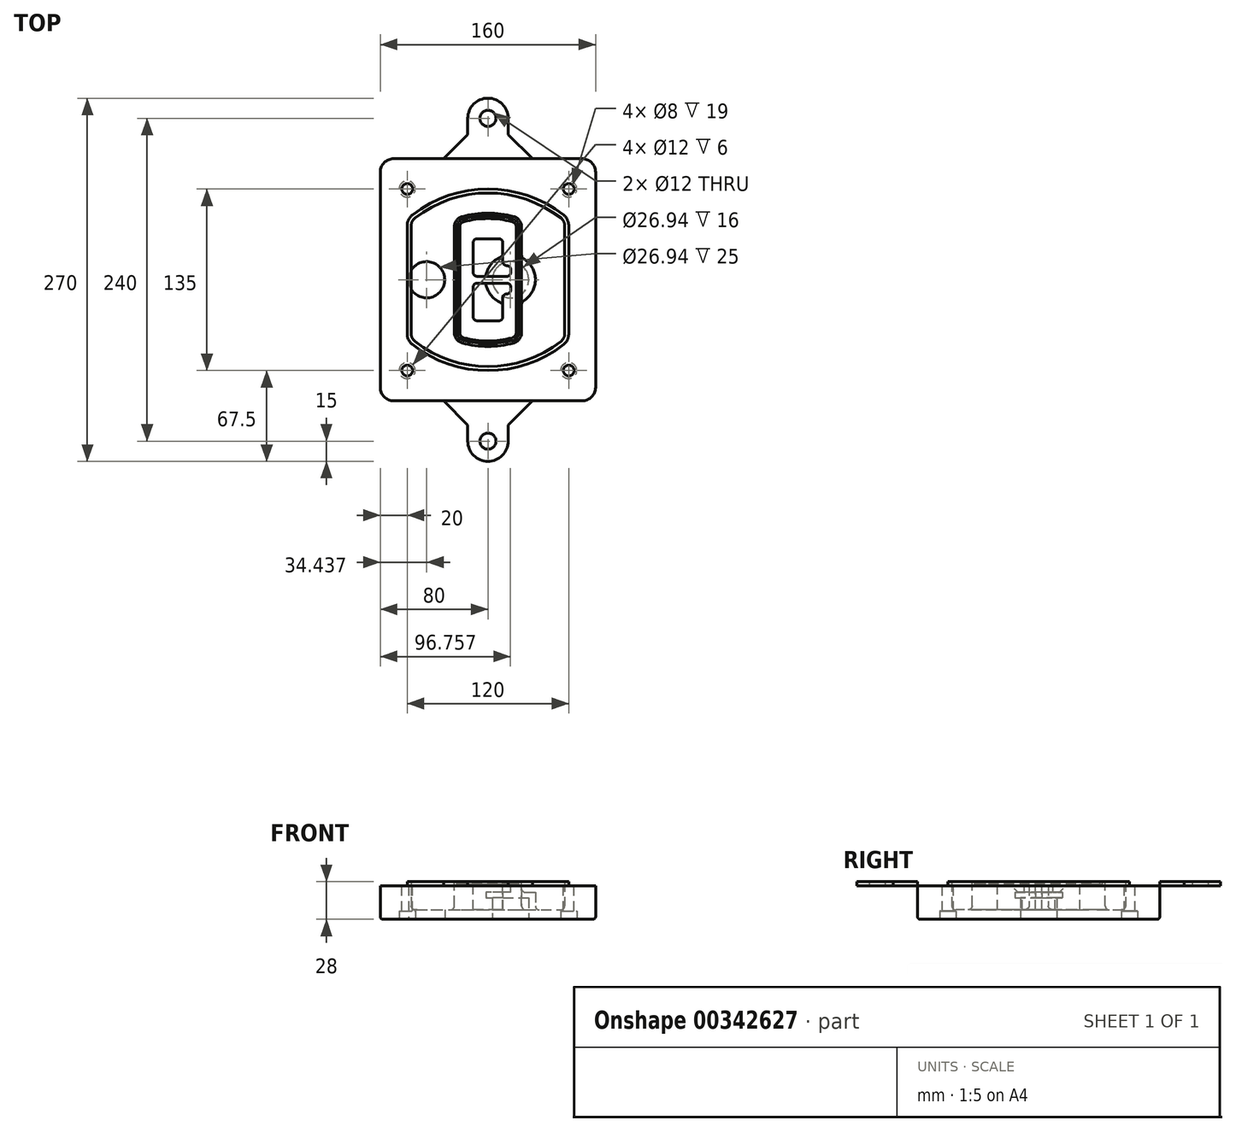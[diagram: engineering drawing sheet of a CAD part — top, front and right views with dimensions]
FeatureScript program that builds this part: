
annotation { "Feature Type Name" : "Feature", "Feature Type Description" : "" }
export const myFeature = defineFeature(function(context is Context, id is Id, definition is map)
    precondition{}
    {
        {
            var Q0;
            Q0=qCreatedBy(makeId("Top.planeOp"),FACE);
            var sketch = newSketch(context, id + "F0", { "sketchPlane" : qUnion([Q0])});
            skPoint(sketch, "E0.rect.middle", {"position": v(0, 0) * mm});
            skLineSegment(sketch, "E1.bottom", {"start": v(-70, -90) * mm, "end": v(70, -90) * mm});
            skLineSegment(sketch, "E1.top", {"start": v(-70, 90) * mm, "end": v(70, 90) * mm});
            skLineSegment(sketch, "E1.left", {"start": v(-80, -80) * mm, "end": v(-80, 80) * mm});
            skLineSegment(sketch, "E1.right", {"start": v(80, -80) * mm, "end": v(80, 80) * mm});
            skLineSegment(sketch, "E2", {"start": v(-80, 90) * mm, "end": v(80, -90) * mm, "construction": true});
            skLineSegment(sketch, "E3", {"start": v(80, 90) * mm, "end": v(-80, -90) * mm, "construction": true});
            skCircle(sketch, "E4", {"center": v(-60, 67.5) * mm, "radius": 4 * mm});
            skCircle(sketch, "E5", {"center": v(60, 67.5) * mm, "radius": 4 * mm});
            skCircle(sketch, "E6", {"center": v(60, -67.5) * mm, "radius": 4 * mm});
            skCircle(sketch, "E7", {"center": v(-60, -67.5) * mm, "radius": 4 * mm});
            skLineSegment(sketch, "E8", {"start": v(-60, 67.5) * mm, "end": v(60, 67.5) * mm, "construction": true});
            skLineSegment(sketch, "E9", {"start": v(60, 67.5) * mm, "end": v(60, -67.5) * mm, "construction": true});
            skLineSegment(sketch, "E10", {"start": v(60, -67.5) * mm, "end": v(-60, -67.5) * mm, "construction": true});
            skLineSegment(sketch, "E11", {"start": v(-60, -67.5) * mm, "end": v(-60, 67.5) * mm, "construction": true});
            skLineSegment(sketch, "E12", {"start": v(-60, 40.3) * mm, "end": v(-60, -40.3) * mm});
            skLineSegment(sketch, "E13", {"start": v(60, 40.3) * mm, "end": v(60, -40.3) * mm});
            skArc(sketch, "E14", {"start": v(56.15, 48.18) * mm, "mid": v(0, 67.5) * mm, "end": v(-56.15, 48.18) * mm});
            skArc(sketch, "E15", {"start": v(-56.15, -48.18) * mm, "mid": v(0, -67.5) * mm, "end": v(56.15, -48.18) * mm});
            skLineSegment(sketch, "E16", {"start": v(-60, 0) * mm, "end": v(60, 0) * mm, "construction": true});
            skPoint(sketch, "E17.visualSharp", {"position": v(-60, -45) * mm});
            skArc(sketch, "E17.filletArc", {"start": v(-60, -40.3) * mm, "mid": v(-58.99, -44.68) * mm, "end": v(-56.15, -48.18) * mm});
            skPoint(sketch, "E18.visualSharp", {"position": v(-60, 45) * mm});
            skArc(sketch, "E18.filletArc", {"start": v(-56.15, 48.18) * mm, "mid": v(-58.99, 44.68) * mm, "end": v(-60, 40.3) * mm});
            skPoint(sketch, "E19.visualSharp", {"position": v(60, 45) * mm});
            skArc(sketch, "E19.filletArc", {"start": v(60, 40.3) * mm, "mid": v(58.99, 44.68) * mm, "end": v(56.15, 48.18) * mm});
            skPoint(sketch, "E20.visualSharp", {"position": v(60, -45) * mm});
            skArc(sketch, "E20.filletArc", {"start": v(56.15, -48.18) * mm, "mid": v(58.99, -44.68) * mm, "end": v(60, -40.3) * mm});
            skPoint(sketch, "E21.visualSharp", {"position": v(-80, 90) * mm});
            skArc(sketch, "E21.filletArc", {"start": v(-70, 90) * mm, "mid": v(-77.07, 87.07) * mm, "end": v(-80, 80) * mm});
            skPoint(sketch, "E22.visualSharp", {"position": v(80, 90) * mm});
            skArc(sketch, "E22.filletArc", {"start": v(80, 80) * mm, "mid": v(77.07, 87.07) * mm, "end": v(70, 90) * mm});
            skPoint(sketch, "E23.visualSharp", {"position": v(80, -90) * mm});
            skArc(sketch, "E23.filletArc", {"start": v(70, -90) * mm, "mid": v(77.07, -87.07) * mm, "end": v(80, -80) * mm});
            skPoint(sketch, "E24.visualSharp", {"position": v(-80, -90) * mm});
            skArc(sketch, "E24.filletArc", {"start": v(-80, -80) * mm, "mid": v(-77.07, -87.07) * mm, "end": v(-70, -90) * mm});
            skArc(sketch, "E25.0", {"start": v(57, 40.3) * mm, "mid": v(56.3, 43.36) * mm, "end": v(54.3, 45.81) * mm});
            skLineSegment(sketch, "E25.1", {"start": v(57, 40.3) * mm, "end": v(57, -40.3) * mm});
            skArc(sketch, "E25.2", {"start": v(54.3, -45.81) * mm, "mid": v(56.3, -43.36) * mm, "end": v(57, -40.3) * mm});
            skArc(sketch, "E25.3", {"start": v(-54.3, -45.81) * mm, "mid": v(0, -64.5) * mm, "end": v(54.3, -45.81) * mm});
            skArc(sketch, "E25.4", {"start": v(-57, -40.3) * mm, "mid": v(-56.3, -43.36) * mm, "end": v(-54.3, -45.81) * mm});
            skArc(sketch, "E25.5", {"start": v(54.3, 45.81) * mm, "mid": v(0, 64.5) * mm, "end": v(-54.3, 45.81) * mm});
            skLineSegment(sketch, "E25.6", {"start": v(-57, 40.3) * mm, "end": v(-57, -40.3) * mm});
            skArc(sketch, "E25.7", {"start": v(-54.3, 45.81) * mm, "mid": v(-56.3, 43.36) * mm, "end": v(-57, 40.3) * mm});
            skArc(sketch, "E26.0", {"start": v(-58.62, 51.33) * mm, "mid": v(-62.58, 46.43) * mm, "end": v(-64, 40.3) * mm});
            skArc(sketch, "E26.1", {"start": v(58.62, 51.33) * mm, "mid": v(0, 71.5) * mm, "end": v(-58.62, 51.33) * mm});
            skArc(sketch, "E26.2", {"start": v(64, 40.3) * mm, "mid": v(62.58, 46.43) * mm, "end": v(58.62, 51.33) * mm});
            skLineSegment(sketch, "E26.3", {"start": v(64, 40.3) * mm, "end": v(64, -40.3) * mm});
            skArc(sketch, "E26.4", {"start": v(58.62, -51.33) * mm, "mid": v(62.58, -46.43) * mm, "end": v(64, -40.3) * mm});
            skLineSegment(sketch, "E26.5", {"start": v(-64, 40.3) * mm, "end": v(-64, -40.3) * mm});
            skArc(sketch, "E26.6", {"start": v(-58.62, -51.33) * mm, "mid": v(0, -71.5) * mm, "end": v(58.62, -51.33) * mm});
            skArc(sketch, "E26.7", {"start": v(-64, -40.3) * mm, "mid": v(-62.58, -46.43) * mm, "end": v(-58.62, -51.33) * mm});
            skSolve(sketch);
        }
        {
            var Q0;
            Q0=makeQuery(id+"F0.imprint","IMPRINT",FACE,{"disambiguationData":[TD([[makeQuery(id+"F0.imprint","IMPRINT",EDGE,{"derivedFrom":sQuery(id+"F0.wireOp",EDGE,"E1.bottom")}),1.0]])]});
            var Q1;
            Q1=makeQuery(id+"F0.imprint","IMPRINT",FACE,{"disambiguationData":[TD([[makeQuery(id+"F0.imprint","IMPRINT",EDGE,{"derivedFrom":sQuery(id+"F0.wireOp",EDGE,"E12")}),1.0]])]});
            var Q2;
            Q2=makeQuery(id+"F0.imprint","IMPRINT",FACE,{"disambiguationData":[TD([[makeQuery(id+"F0.imprint","IMPRINT",EDGE,{"derivedFrom":sQuery(id+"F0.wireOp",EDGE,"E25.0")}),1.0]])]});
            var Q3;
            Q3=makeQuery(id+"F0.imprint","IMPRINT",FACE,{"disambiguationData":[TD([[makeQuery(id+"F0.imprint","IMPRINT",EDGE,{"derivedFrom":sQuery(id+"F0.wireOp",EDGE,"E12")}),-1.0]])]});
            extrude(context, id + "F1", {"entities" : qUnion([Q0, Q1, Q2, Q3]), "oppositeDirection" : true, "depth" : 25 * mm});
        }
        {
            var Q0;
            Q0=makeQuery(id+"F0.imprint","IMPRINT",FACE,{"disambiguationData":[TD([[makeQuery(id+"F0.imprint","IMPRINT",EDGE,{"derivedFrom":sQuery(id+"F0.wireOp",EDGE,"E12")}),1.0]])]});
            extrude(context, id + "F2", {"entities" : qUnion([Q0]), "operationType" : NewBodyOperationType.ADD, "depth" : 3 * mm});
        }
        {
            var Q0;
            Q0=makeQuery(id+"F0.imprint","IMPRINT",FACE,{"disambiguationData":[TD([[makeQuery(id+"F0.imprint","IMPRINT",EDGE,{"derivedFrom":sQuery(id+"F0.wireOp",EDGE,"E25.0")}),1.0]])]});
            extrude(context, id + "F3", {"entities" : qUnion([Q0]), "operationType" : NewBodyOperationType.REMOVE, "oppositeDirection" : true, "depth" : 18 * mm});
        }
        {
            var Q0;
            Q0=makeQuery(id+"F2.opExtrude","CAP_FACE",FACE,{"disambiguationData":[OSD([sQuery(id+"F0.wireOp",EDGE,"E12"),sQuery(id+"F0.wireOp",EDGE,"E13"),sQuery(id+"F0.wireOp",EDGE,"E14"),sQuery(id+"F0.wireOp",EDGE,"E15"),sQuery(id+"F0.wireOp",EDGE,"E17.filletArc"),sQuery(id+"F0.wireOp",EDGE,"E18.filletArc"),sQuery(id+"F0.wireOp",EDGE,"E19.filletArc"),sQuery(id+"F0.wireOp",EDGE,"E20.filletArc"),sQuery(id+"F0.wireOp",EDGE,"E25.0"),sQuery(id+"F0.wireOp",EDGE,"E25.1"),sQuery(id+"F0.wireOp",EDGE,"E25.2"),sQuery(id+"F0.wireOp",EDGE,"E25.3"),sQuery(id+"F0.wireOp",EDGE,"E25.4"),sQuery(id+"F0.wireOp",EDGE,"E25.5"),sQuery(id+"F0.wireOp",EDGE,"E25.6"),sQuery(id+"F0.wireOp",EDGE,"E25.7")])],"isStart":false});
            var sketch = newSketch(context, id + "F4", { "sketchPlane" : qUnion([Q0])});
            skArc(sketch, "E27.0", {"start": v(-19.08, -46.97) * mm, "mid": v(0, -49.5) * mm, "end": v(19.08, -46.97) * mm});
            skArc(sketch, "E28.0", {"start": v(19.08, 46.97) * mm, "mid": v(0, 49.5) * mm, "end": v(-19.08, 46.97) * mm});
            skLineSegment(sketch, "E29", {"start": v(-25, 39.25) * mm, "end": v(-25, -39.25) * mm});
            skLineSegment(sketch, "E30", {"start": v(25, 39.25) * mm, "end": v(25, -39.25) * mm});
            skLineSegment(sketch, "E31", {"start": v(-25, 45.1) * mm, "end": v(25, 45.1) * mm, "construction": true});
            skLineSegment(sketch, "E32", {"start": v(-25, -45.1) * mm, "end": v(25, -45.1) * mm, "construction": true});
            skPoint(sketch, "E33.visualSharp", {"position": v(-25, 45.1) * mm});
            skArc(sketch, "E33.filletArc", {"start": v(-19.08, 46.97) * mm, "mid": v(-23.35, 44.11) * mm, "end": v(-25, 39.25) * mm});
            skPoint(sketch, "E34.visualSharp", {"position": v(25, 45.1) * mm});
            skArc(sketch, "E34.filletArc", {"start": v(25, 39.25) * mm, "mid": v(23.35, 44.11) * mm, "end": v(19.08, 46.97) * mm});
            skPoint(sketch, "E35.visualSharp", {"position": v(25, -45.1) * mm});
            skArc(sketch, "E35.filletArc", {"start": v(19.08, -46.97) * mm, "mid": v(23.35, -44.11) * mm, "end": v(25, -39.25) * mm});
            skPoint(sketch, "E36.visualSharp", {"position": v(-25, -45.1) * mm});
            skArc(sketch, "E36.filletArc", {"start": v(-25, -39.25) * mm, "mid": v(-23.35, -44.11) * mm, "end": v(-19.08, -46.97) * mm});
            skArc(sketch, "E37.0", {"start": v(54.3, 45.81) * mm, "mid": v(0, 64.5) * mm, "end": v(-54.3, 45.81) * mm});
            skArc(sketch, "E37.1", {"start": v(-54.3, 45.81) * mm, "mid": v(-56.3, 43.36) * mm, "end": v(-57, 40.3) * mm});
            skLineSegment(sketch, "E37.2", {"start": v(-57, 40.3) * mm, "end": v(-57, -40.3) * mm});
            skArc(sketch, "E37.3", {"start": v(-57, -40.3) * mm, "mid": v(-56.3, -43.36) * mm, "end": v(-54.3, -45.81) * mm});
            skArc(sketch, "E37.4", {"start": v(-54.3, -45.81) * mm, "mid": v(0, -64.5) * mm, "end": v(54.3, -45.81) * mm});
            skArc(sketch, "E37.5", {"start": v(54.3, -45.81) * mm, "mid": v(56.3, -43.36) * mm, "end": v(57, -40.3) * mm});
            skLineSegment(sketch, "E37.6", {"start": v(57, 40.3) * mm, "end": v(57, -40.3) * mm});
            skArc(sketch, "E37.7", {"start": v(57, 40.3) * mm, "mid": v(56.3, 43.36) * mm, "end": v(54.3, 45.81) * mm});
            skLineSegment(sketch, "E38.0", {"start": v(23, 39.25) * mm, "end": v(23, -39.25) * mm});
            skArc(sketch, "E38.1", {"start": v(18.56, -45.04) * mm, "mid": v(21.76, -42.9) * mm, "end": v(23, -39.25) * mm});
            skArc(sketch, "E38.2", {"start": v(-18.56, -45.04) * mm, "mid": v(0, -47.5) * mm, "end": v(18.56, -45.04) * mm});
            skArc(sketch, "E38.3", {"start": v(-23, -39.25) * mm, "mid": v(-21.76, -42.9) * mm, "end": v(-18.56, -45.04) * mm});
            skLineSegment(sketch, "E38.4", {"start": v(-23, 39.25) * mm, "end": v(-23, -39.25) * mm});
            skArc(sketch, "E38.5", {"start": v(23, 39.25) * mm, "mid": v(21.76, 42.9) * mm, "end": v(18.56, 45.04) * mm});
            skArc(sketch, "E38.6", {"start": v(-18.56, 45.04) * mm, "mid": v(-21.76, 42.9) * mm, "end": v(-23, 39.25) * mm});
            skArc(sketch, "E38.7", {"start": v(18.56, 45.04) * mm, "mid": v(0, 47.5) * mm, "end": v(-18.56, 45.04) * mm});
            skArc(sketch, "E39.0", {"start": v(21, 39.25) * mm, "mid": v(20.18, 41.68) * mm, "end": v(18.04, 43.1) * mm});
            skLineSegment(sketch, "E39.1", {"start": v(21, 39.25) * mm, "end": v(21, -39.25) * mm});
            skArc(sketch, "E39.2", {"start": v(18.04, -43.1) * mm, "mid": v(20.18, -41.68) * mm, "end": v(21, -39.25) * mm});
            skArc(sketch, "E39.3", {"start": v(-18.04, -43.1) * mm, "mid": v(0, -45.5) * mm, "end": v(18.04, -43.1) * mm});
            skArc(sketch, "E39.4", {"start": v(-21, -39.25) * mm, "mid": v(-20.18, -41.68) * mm, "end": v(-18.04, -43.1) * mm});
            skArc(sketch, "E39.5", {"start": v(18.04, 43.1) * mm, "mid": v(0, 45.5) * mm, "end": v(-18.04, 43.1) * mm});
            skLineSegment(sketch, "E39.6", {"start": v(-21, 39.25) * mm, "end": v(-21, -39.25) * mm});
            skArc(sketch, "E39.7", {"start": v(-18.04, 43.1) * mm, "mid": v(-20.18, 41.68) * mm, "end": v(-21, 39.25) * mm});
            skLineSegment(sketch, "E40", {"start": v(-25, 0) * mm, "end": v(25, 0) * mm, "construction": true});
            skLineSegment(sketch, "E41", {"start": v(-11, 5.5) * mm, "end": v(-11, 27.5) * mm});
            skLineSegment(sketch, "E42", {"start": v(-8, 30.5) * mm, "end": v(8, 30.5) * mm});
            skLineSegment(sketch, "E43", {"start": v(11, 27.5) * mm, "end": v(11, 13.5) * mm});
            skLineSegment(sketch, "E44", {"start": v(14, 10.5) * mm, "end": v(14, 10.5) * mm});
            skLineSegment(sketch, "E45", {"start": v(17, 7.5) * mm, "end": v(17, 5.5) * mm});
            skLineSegment(sketch, "E46", {"start": v(14, 2.5) * mm, "end": v(-8, 2.5) * mm});
            skPoint(sketch, "E47.visualSharp", {"position": v(-11, 30.5) * mm});
            skArc(sketch, "E47.filletArc", {"start": v(-8, 30.5) * mm, "mid": v(-10.12, 29.62) * mm, "end": v(-11, 27.5) * mm});
            skPoint(sketch, "E48.visualSharp", {"position": v(11, 30.5) * mm});
            skArc(sketch, "E48.filletArc", {"start": v(11, 27.5) * mm, "mid": v(10.12, 29.62) * mm, "end": v(8, 30.5) * mm});
            skPoint(sketch, "E49.visualSharp", {"position": v(11, 10.5) * mm});
            skArc(sketch, "E49.filletArc", {"start": v(11, 13.5) * mm, "mid": v(11.88, 11.38) * mm, "end": v(14, 10.5) * mm});
            skPoint(sketch, "E50.visualSharp", {"position": v(17, 10.5) * mm});
            skArc(sketch, "E50.filletArc", {"start": v(17, 7.5) * mm, "mid": v(16.12, 9.62) * mm, "end": v(14, 10.5) * mm});
            skPoint(sketch, "E51.visualSharp", {"position": v(17, 2.5) * mm});
            skArc(sketch, "E51.filletArc", {"start": v(14, 2.5) * mm, "mid": v(16.12, 3.38) * mm, "end": v(17, 5.5) * mm});
            skPoint(sketch, "E52.visualSharp", {"position": v(-11, 2.5) * mm});
            skArc(sketch, "E52.filletArc", {"start": v(-11, 5.5) * mm, "mid": v(-10.12, 3.38) * mm, "end": v(-8, 2.5) * mm});
            skLineSegment(sketch, "E53.0.MirrorCS", {"start": v(14, -2.5) * mm, "end": v(-8, -2.5) * mm});
            skArc(sketch, "E54.0.MirrorCS", {"start": v(-11, -5.5) * mm, "mid": v(-10.12, -3.38) * mm, "end": v(-8, -2.5) * mm});
            skLineSegment(sketch, "E55.0.MirrorCS", {"start": v(-11, -5.5) * mm, "end": v(-11, -27.5) * mm});
            skArc(sketch, "E56.0.MirrorCS", {"start": v(-8, -30.5) * mm, "mid": v(-10.12, -29.62) * mm, "end": v(-11, -27.5) * mm});
            skLineSegment(sketch, "E57.0.MirrorCS", {"start": v(-8, -30.5) * mm, "end": v(8, -30.5) * mm});
            skArc(sketch, "E58.0.MirrorCS", {"start": v(11, -27.5) * mm, "mid": v(10.12, -29.62) * mm, "end": v(8, -30.5) * mm});
            skLineSegment(sketch, "E59.0.MirrorCS", {"start": v(11, -27.5) * mm, "end": v(11, -13.5) * mm});
            skArc(sketch, "E60.0.MirrorCS", {"start": v(11, -13.5) * mm, "mid": v(11.88, -11.38) * mm, "end": v(14, -10.5) * mm});
            skArc(sketch, "E61.0.MirrorCS", {"start": v(17, -7.5) * mm, "mid": v(16.12, -9.62) * mm, "end": v(14, -10.5) * mm});
            skLineSegment(sketch, "E62.0.MirrorCS", {"start": v(17, -7.5) * mm, "end": v(17, -5.5) * mm});
            skArc(sketch, "E63.0.MirrorCS", {"start": v(14, -2.5) * mm, "mid": v(16.12, -3.38) * mm, "end": v(17, -5.5) * mm});
            skSolve(sketch);
        }
        {
            var Q0;
            Q0=makeQuery(id+"F4.imprint","IMPRINT",FACE,{"disambiguationData":[TD([[makeQuery(id+"F4.imprint","IMPRINT",EDGE,{"derivedFrom":sQuery(id+"F4.wireOp",EDGE,"E27.0")}),1.0]])]});
            var Q1;
            Q1=makeQuery(id+"F4.imprint","IMPRINT",FACE,{"disambiguationData":[TD([[makeQuery(id+"F4.imprint","IMPRINT",EDGE,{"derivedFrom":sQuery(id+"F4.wireOp",EDGE,"E38.0")}),-1.0]])]});
            var Q2;
            Q2=makeQuery(id+"F4.imprint","IMPRINT",FACE,{"disambiguationData":[TD([[makeQuery(id+"F4.imprint","IMPRINT",EDGE,{"derivedFrom":sQuery(id+"F4.wireOp",EDGE,"E39.0")}),1.0]])]});
            extrude(context, id + "F5", {"entities" : qUnion([Q0, Q1, Q2]), "operationType" : NewBodyOperationType.ADD, "endBound" : BoundingType.UP_TO_NEXT, "oppositeDirection" : true, "depth" : 25 * mm});
        }
        {
            var Q0;
            Q0=makeQuery(id+"F4.imprint","IMPRINT",FACE,{"disambiguationData":[TD([[makeQuery(id+"F4.imprint","IMPRINT",EDGE,{"derivedFrom":sQuery(id+"F4.wireOp",EDGE,"E38.0")}),-1.0]])]});
            extrude(context, id + "F6", {"entities" : qUnion([Q0]), "operationType" : NewBodyOperationType.REMOVE, "oppositeDirection" : true, "depth" : 2 * mm});
        }
        {
            var Q0;
            Q0=makeQuery(id+"F1.opExtrude","CAP_FACE",FACE,{"disambiguationData":[OSD([sQuery(id+"F0.wireOp",EDGE,"E1.bottom"),sQuery(id+"F0.wireOp",EDGE,"E1.top"),sQuery(id+"F0.wireOp",EDGE,"E1.left"),sQuery(id+"F0.wireOp",EDGE,"E1.right"),sQuery(id+"F0.wireOp",EDGE,"E4"),sQuery(id+"F0.wireOp",EDGE,"E5"),sQuery(id+"F0.wireOp",EDGE,"E6"),sQuery(id+"F0.wireOp",EDGE,"E7"),sQuery(id+"F0.wireOp",EDGE,"E21.filletArc"),sQuery(id+"F0.wireOp",EDGE,"E22.filletArc"),sQuery(id+"F0.wireOp",EDGE,"E23.filletArc"),sQuery(id+"F0.wireOp",EDGE,"E24.filletArc")])],"isStart":false});
            var sketch = newSketch(context, id + "F7", { "sketchPlane" : qUnion([Q0])});
            skCircle(sketch, "E64", {"center": v(16.76, 0) * mm, "radius": 13.47 * mm});
            skCircle(sketch, "E65", {"center": v(-45.56, 0) * mm, "radius": 13.47 * mm});
            skLineSegment(sketch, "E66", {"start": v(80, 0) * mm, "end": v(-80, 0) * mm});
            skCircle(sketch, "E67", {"center": v(16.76, 0) * mm, "radius": 18.47 * mm});
            skCircle(sketch, "E68", {"center": v(60, -67.5) * mm, "radius": 6 * mm});
            skCircle(sketch, "E69", {"center": v(-60, -67.5) * mm, "radius": 6 * mm});
            skCircle(sketch, "E70", {"center": v(-60, 67.5) * mm, "radius": 6 * mm});
            skCircle(sketch, "E71", {"center": v(60, 67.5) * mm, "radius": 6 * mm});
            skSolve(sketch);
        }
        {
            var Q0;
            {var subQ1=sQuery(id+"F7.wireOp",EDGE,"E66");var subQ4=sQuery(id+"F7.wireOp",EDGE,"E64");var subQ6=makeQuery(id+"F7.imprint","INTERSECT",VERTEX,{"disambiguationData":[OD(0.0)],"derivedFrom":[subQ4,subQ1]});Q0=makeQuery(id+"F7.imprint","IMPRINT",FACE,{"disambiguationData":[TD([[makeQuery(id+"F7.imprint","IMPRINT",EDGE,{"disambiguationData":[TD([[subQ6,-1.0]])],"derivedFrom":subQ4}),-1.0]])]});}
            var Q1;
            {var subQ0=sQuery(id+"F7.wireOp",EDGE,"E66");var subQ1=sQuery(id+"F7.wireOp",EDGE,"E64");var subQ3=makeQuery(id+"F7.imprint","INTERSECT",VERTEX,{"disambiguationData":[OD(0.0)],"derivedFrom":[subQ1,subQ0]});Q1=makeQuery(id+"F7.imprint","IMPRINT",FACE,{"disambiguationData":[TD([[makeQuery(id+"F7.imprint","IMPRINT",EDGE,{"disambiguationData":[TD([[subQ3,-1.0]])],"derivedFrom":subQ1}),1.0]])]});}
            var Q2;
            {var subQ0=sQuery(id+"F7.wireOp",EDGE,"E66");var subQ1=sQuery(id+"F7.wireOp",EDGE,"E64");var subQ3=makeQuery(id+"F7.imprint","INTERSECT",VERTEX,{"disambiguationData":[OD(0.0)],"derivedFrom":[subQ1,subQ0]});Q2=makeQuery(id+"F7.imprint","IMPRINT",FACE,{"disambiguationData":[TD([[makeQuery(id+"F7.imprint","IMPRINT",EDGE,{"disambiguationData":[TD([[subQ3,1.0]])],"derivedFrom":subQ1}),1.0]])]});}
            var Q3;
            {var subQ1=sQuery(id+"F7.wireOp",EDGE,"E66");var subQ4=sQuery(id+"F7.wireOp",EDGE,"E64");var subQ6=makeQuery(id+"F7.imprint","INTERSECT",VERTEX,{"disambiguationData":[OD(0.0)],"derivedFrom":[subQ4,subQ1]});Q3=makeQuery(id+"F7.imprint","IMPRINT",FACE,{"disambiguationData":[TD([[makeQuery(id+"F7.imprint","IMPRINT",EDGE,{"disambiguationData":[TD([[subQ6,1.0]])],"derivedFrom":subQ4}),-1.0]])]});}
            extrude(context, id + "F8", {"entities" : qUnion([Q0, Q1, Q2, Q3]), "operationType" : NewBodyOperationType.ADD, "oppositeDirection" : true, "depth" : 20 * mm});
        }
        {
            var Q0;
            {var subQ0=sQuery(id+"F7.wireOp",EDGE,"E66");var subQ1=sQuery(id+"F7.wireOp",EDGE,"E64");var subQ3=makeQuery(id+"F7.imprint","INTERSECT",VERTEX,{"disambiguationData":[OD(0.0)],"derivedFrom":[subQ1,subQ0]});Q0=makeQuery(id+"F7.imprint","IMPRINT",FACE,{"disambiguationData":[TD([[makeQuery(id+"F7.imprint","IMPRINT",EDGE,{"disambiguationData":[TD([[subQ3,-1.0]])],"derivedFrom":subQ1}),1.0]])]});}
            var Q1;
            {var subQ0=sQuery(id+"F7.wireOp",EDGE,"E66");var subQ1=sQuery(id+"F7.wireOp",EDGE,"E64");var subQ3=makeQuery(id+"F7.imprint","INTERSECT",VERTEX,{"disambiguationData":[OD(0.0)],"derivedFrom":[subQ1,subQ0]});Q1=makeQuery(id+"F7.imprint","IMPRINT",FACE,{"disambiguationData":[TD([[makeQuery(id+"F7.imprint","IMPRINT",EDGE,{"disambiguationData":[TD([[subQ3,1.0]])],"derivedFrom":subQ1}),1.0]])]});}
            extrude(context, id + "F9", {"entities" : qUnion([Q0, Q1]), "operationType" : NewBodyOperationType.REMOVE, "oppositeDirection" : true, "depth" : 16 * mm});
        }
        {
            var Q0;
            {var subQ0=sQuery(id+"F7.wireOp",EDGE,"E66");var subQ1=sQuery(id+"F7.wireOp",EDGE,"E65");var subQ3=makeQuery(id+"F7.imprint","INTERSECT",VERTEX,{"disambiguationData":[OD(0.0)],"derivedFrom":[subQ1,subQ0]});Q0=makeQuery(id+"F7.imprint","IMPRINT",FACE,{"disambiguationData":[TD([[makeQuery(id+"F7.imprint","IMPRINT",EDGE,{"disambiguationData":[TD([[subQ3,-1.0]])],"derivedFrom":subQ1}),1.0]])]});}
            var Q1;
            {var subQ0=sQuery(id+"F7.wireOp",EDGE,"E66");var subQ1=sQuery(id+"F7.wireOp",EDGE,"E65");var subQ3=makeQuery(id+"F7.imprint","INTERSECT",VERTEX,{"disambiguationData":[OD(0.0)],"derivedFrom":[subQ1,subQ0]});Q1=makeQuery(id+"F7.imprint","IMPRINT",FACE,{"disambiguationData":[TD([[makeQuery(id+"F7.imprint","IMPRINT",EDGE,{"disambiguationData":[TD([[subQ3,1.0]])],"derivedFrom":subQ1}),1.0]])]});}
            extrude(context, id + "F10", {"entities" : qUnion([Q0, Q1]), "operationType" : NewBodyOperationType.REMOVE, "oppositeDirection" : true, "depth" : 25 * mm});
        }
        {
            var Q0;
            Q0=makeQuery(id+"F7.imprint","IMPRINT",FACE,{"disambiguationData":[TD([[makeQuery(id+"F7.imprint","IMPRINT",EDGE,{"derivedFrom":sQuery(id+"F7.wireOp",EDGE,"E68")}),1.0]])]});
            var Q1;
            Q1=makeQuery(id+"F7.imprint","IMPRINT",FACE,{"disambiguationData":[TD([[makeQuery(id+"F7.imprint","IMPRINT",EDGE,{"derivedFrom":makeQuery(id+"F1.opExtrude","CAP_EDGE",EDGE,{"disambiguationData":[OSD([sQuery(id+"F0.wireOp",EDGE,"E5")])],"isStart":false})}),-1.0]])]});
            var Q2;
            Q2=makeQuery(id+"F7.imprint","IMPRINT",FACE,{"disambiguationData":[TD([[makeQuery(id+"F7.imprint","IMPRINT",EDGE,{"derivedFrom":sQuery(id+"F7.wireOp",EDGE,"E69")}),1.0]])]});
            var Q3;
            Q3=makeQuery(id+"F7.imprint","IMPRINT",FACE,{"disambiguationData":[TD([[makeQuery(id+"F7.imprint","IMPRINT",EDGE,{"derivedFrom":makeQuery(id+"F1.opExtrude","CAP_EDGE",EDGE,{"disambiguationData":[OSD([sQuery(id+"F0.wireOp",EDGE,"E4")])],"isStart":false})}),-1.0]])]});
            var Q4;
            Q4=makeQuery(id+"F7.imprint","IMPRINT",FACE,{"disambiguationData":[TD([[makeQuery(id+"F7.imprint","IMPRINT",EDGE,{"derivedFrom":sQuery(id+"F7.wireOp",EDGE,"E70")}),1.0]])]});
            var Q5;
            Q5=makeQuery(id+"F7.imprint","IMPRINT",FACE,{"disambiguationData":[TD([[makeQuery(id+"F7.imprint","IMPRINT",EDGE,{"derivedFrom":makeQuery(id+"F1.opExtrude","CAP_EDGE",EDGE,{"disambiguationData":[OSD([sQuery(id+"F0.wireOp",EDGE,"E7")])],"isStart":false})}),-1.0]])]});
            var Q6;
            Q6=makeQuery(id+"F7.imprint","IMPRINT",FACE,{"disambiguationData":[TD([[makeQuery(id+"F7.imprint","IMPRINT",EDGE,{"derivedFrom":sQuery(id+"F7.wireOp",EDGE,"E71")}),1.0]])]});
            var Q7;
            Q7=makeQuery(id+"F7.imprint","IMPRINT",FACE,{"disambiguationData":[TD([[makeQuery(id+"F7.imprint","IMPRINT",EDGE,{"derivedFrom":makeQuery(id+"F1.opExtrude","CAP_EDGE",EDGE,{"disambiguationData":[OSD([sQuery(id+"F0.wireOp",EDGE,"E6")])],"isStart":false})}),-1.0]])]});
            extrude(context, id + "F11", {"entities" : qUnion([Q0, Q1, Q2, Q3, Q4, Q5, Q6, Q7]), "operationType" : NewBodyOperationType.REMOVE, "oppositeDirection" : true, "depth" : 6 * mm});
        }
        {
            var Q0;
            Q0=makeQuery(id+"F9.boolean.opBoolean","COPY",FACE,{"derivedFrom":makeQuery(id+"F9.opExtrude","CAP_FACE",FACE,{"disambiguationData":[OSD([sQuery(id+"F7.wireOp",EDGE,"E64")])],"isStart":false})});
            var sketch = newSketch(context, id + "F12", { "sketchPlane" : qUnion([Q0])});
            skArc(sketch, "E72.0", {"start": v(11, 17.55) * mm, "mid": v(2.57, 11.82) * mm, "end": v(-1.54, 2.5) * mm});
            skArc(sketch, "E72.1", {"start": v(-1.54, -2.5) * mm, "mid": v(2.57, -11.82) * mm, "end": v(11, -17.55) * mm});
            skLineSegment(sketch, "E73", {"start": v(-1.54, -2.5) * mm, "end": v(14, -2.5) * mm});
            skLineSegment(sketch, "E74.0", {"start": v(14, 2.5) * mm, "end": v(-1.54, 2.5) * mm});
            skArc(sketch, "E74.1", {"start": v(14, 2.5) * mm, "mid": v(16.12, 3.38) * mm, "end": v(17, 5.5) * mm});
            skLineSegment(sketch, "E74.2", {"start": v(17, 7.5) * mm, "end": v(17, 5.5) * mm});
            skArc(sketch, "E74.3", {"start": v(17, 7.5) * mm, "mid": v(16.12, 9.62) * mm, "end": v(14, 10.5) * mm});
            skArc(sketch, "E74.4", {"start": v(11, 13.5) * mm, "mid": v(11.88, 11.38) * mm, "end": v(14, 10.5) * mm});
            skLineSegment(sketch, "E74.5", {"start": v(11, 17.55) * mm, "end": v(11, 13.5) * mm});
            skLineSegment(sketch, "E74.7", {"start": v(14, -2.5) * mm, "end": v(-1.54, -2.5) * mm});
            skArc(sketch, "E74.8", {"start": v(14, -2.5) * mm, "mid": v(16.12, -3.38) * mm, "end": v(17, -5.5) * mm});
            skLineSegment(sketch, "E74.9", {"start": v(17, -7.5) * mm, "end": v(17, -5.5) * mm});
            skArc(sketch, "E74.10", {"start": v(17, -7.5) * mm, "mid": v(16.12, -9.62) * mm, "end": v(14, -10.5) * mm});
            skArc(sketch, "E74.11", {"start": v(11, -13.5) * mm, "mid": v(11.88, -11.38) * mm, "end": v(14, -10.5) * mm});
            skLineSegment(sketch, "E74.12", {"start": v(11, -17.55) * mm, "end": v(11, -13.5) * mm});
            skPoint(sketch, "E75.orphan", {"position": v(11, -27.5) * mm});
            skPoint(sketch, "E76.orphan", {"position": v(-8, -2.5) * mm});
            skPoint(sketch, "E77.orphan", {"position": v(-8, 2.5) * mm});
            skPoint(sketch, "E78.orphan", {"position": v(11, 27.5) * mm});
            skSolve(sketch);
        }
        {
            var Q0;
            {var subQ7=sQuery(id+"F12.wireOp",EDGE,"E72.0");var subQ14=sQuery(id+"F12.wireOp",EDGE,"E72.1");var subQ16=sQuery(id+"F12.wireOp",EDGE,"E74.1");var subQ18=sQuery(id+"F12.wireOp",EDGE,"E74.8");Q0=qUnion([makeQuery(id+"F12.imprint","IMPRINT",FACE,{"disambiguationData":[TD([[makeQuery(id+"F12.imprint","IMPRINT",EDGE,{"derivedFrom":subQ7}),1.0]])]}),makeQuery(id+"F12.imprint","IMPRINT",FACE,{"disambiguationData":[TD([[makeQuery(id+"F12.imprint","IMPRINT",EDGE,{"derivedFrom":subQ14}),1.0]])]}),makeQuery(id+"F12.imprint","IMPRINT",FACE,{"disambiguationData":[TD([[makeQuery(id+"F12.imprint","IMPRINT",EDGE,{"derivedFrom":subQ16}),1.0]])]}),makeQuery(id+"F12.imprint","IMPRINT",FACE,{"disambiguationData":[TD([[makeQuery(id+"F12.imprint","IMPRINT",EDGE,{"derivedFrom":subQ18}),-1.0]])]})]);}
            var Q1;
            Q1=makeQuery(id+"F5.boolean.opBoolean","SPLIT",FACE,{"disambiguationData":[TD([makeQuery(id+"F5.opExtrude","SWEPT_FACE",FACE,{"disambiguationData":[OSD([sQuery(id+"F4.wireOp",EDGE,"E41")])]})])],"derivedFrom":makeQuery(id+"F3.boolean.opBoolean","COPY",FACE,{"derivedFrom":makeQuery(id+"F3.opExtrude","CAP_FACE",FACE,{"disambiguationData":[OSD([sQuery(id+"F0.wireOp",EDGE,"E25.0"),sQuery(id+"F0.wireOp",EDGE,"E25.1"),sQuery(id+"F0.wireOp",EDGE,"E25.2"),sQuery(id+"F0.wireOp",EDGE,"E25.3"),sQuery(id+"F0.wireOp",EDGE,"E25.4"),sQuery(id+"F0.wireOp",EDGE,"E25.5"),sQuery(id+"F0.wireOp",EDGE,"E25.6"),sQuery(id+"F0.wireOp",EDGE,"E25.7")])],"isStart":false})})});
            extrude(context, id + "F13", {"entities" : qUnion([Q0]), "operationType" : NewBodyOperationType.REMOVE, "endBound" : BoundingType.UP_TO_SURFACE, "endBoundEntityFace" : qUnion([Q1]), "depth" : 25 * mm});
        }
        {
            var Q0;
            Q0=makeQuery(id+"F3.boolean.opBoolean","COPY",EDGE,{"derivedFrom":makeQuery(id+"F3.opExtrude","CAP_EDGE",EDGE,{"disambiguationData":[OSD([sQuery(id+"F0.wireOp",EDGE,"E25.6")])],"isStart":false})});
            var Q1;
            Q1=makeQuery(id+"F8.boolean.opBoolean","INTERSECT",EDGE,{"derivedFrom":[makeQuery(id+"F5.opExtrude","SWEPT_FACE",FACE,{"disambiguationData":[OSD([sQuery(id+"F4.wireOp",EDGE,"E30")])]}),makeQuery(id+"F8.opExtrude","CAP_FACE",FACE,{"disambiguationData":[OSD([sQuery(id+"F7.wireOp",EDGE,"E67")])],"isStart":false})]});
            var Q2;
            Q2=makeQuery(id+"F8.boolean.opBoolean","INTERSECT",EDGE,{"disambiguationData":[OD(1.0)],"derivedFrom":[makeQuery(id+"F5.opExtrude","SWEPT_FACE",FACE,{"disambiguationData":[OSD([sQuery(id+"F4.wireOp",EDGE,"E30")])]}),makeQuery(id+"F8.opExtrude","SWEPT_FACE",FACE,{"disambiguationData":[OSD([sQuery(id+"F7.wireOp",EDGE,"E67")])]})]});
            var Q3;
            {var subQ0=sQuery(id+"F4.wireOp",EDGE,"E30");Q3=makeQuery(id+"F8.boolean.opBoolean","SPLIT",EDGE,{"disambiguationData":[TD([makeQuery(id+"F5.opExtrude","SWEPT_FACE",FACE,{"disambiguationData":[OSD([sQuery(id+"F4.wireOp",EDGE,"E35.filletArc")])]})])],"derivedFrom":makeQuery(id+"F5.opExtrude","CAP_EDGE",EDGE,{"disambiguationData":[OSD([subQ0])],"isStart":false})});}
            var Q4;
            {var subQ0=sQuery(id+"F0.wireOp",EDGE,"E25.7");var subQ1=sQuery(id+"F0.wireOp",EDGE,"E25.1");var subQ2=sQuery(id+"F0.wireOp",EDGE,"E25.6");var subQ3=sQuery(id+"F0.wireOp",EDGE,"E25.5");var subQ4=sQuery(id+"F0.wireOp",EDGE,"E25.4");var subQ5=sQuery(id+"F0.wireOp",EDGE,"E25.0");var subQ6=sQuery(id+"F0.wireOp",EDGE,"E25.2");var subQ7=sQuery(id+"F0.wireOp",EDGE,"E25.3");Q4=makeQuery(id+"F8.boolean.opBoolean","INTERSECT",EDGE,{"derivedFrom":[makeQuery(id+"F5.boolean.opBoolean","SPLIT",FACE,{"disambiguationData":[TD([makeQuery(id+"F2.opExtrude","SWEPT_FACE",FACE,{"disambiguationData":[OSD([subQ5])]})])],"derivedFrom":makeQuery(id+"F3.boolean.opBoolean","COPY",FACE,{"derivedFrom":makeQuery(id+"F3.opExtrude","CAP_FACE",FACE,{"disambiguationData":[OSD([subQ5,subQ1,subQ6,subQ7,subQ4,subQ3,subQ2,subQ0])],"isStart":false})})}),makeQuery(id+"F8.opExtrude","SWEPT_FACE",FACE,{"disambiguationData":[OSD([sQuery(id+"F7.wireOp",EDGE,"E67")])]})]});}
            var Q5;
            Q5=makeQuery(id+"F8.boolean.opBoolean","INTERSECT",EDGE,{"disambiguationData":[OD(0.0)],"derivedFrom":[makeQuery(id+"F5.opExtrude","SWEPT_FACE",FACE,{"disambiguationData":[OSD([sQuery(id+"F4.wireOp",EDGE,"E30")])]}),makeQuery(id+"F8.opExtrude","SWEPT_FACE",FACE,{"disambiguationData":[OSD([sQuery(id+"F7.wireOp",EDGE,"E67")])]})]});
            fillet(context, id + "F14", {"entities" : qUnion([Q0, Q1, Q2, Q3, Q4, Q5]), "radius" : 3 * mm, "tangentPropagation" : true, "allowEdgeOverflow" : false});
        }
        {
            var Q0;
            Q0=makeQuery(id+"F1.opExtrude","CAP_EDGE",EDGE,{"disambiguationData":[OSD([sQuery(id+"F0.wireOp",EDGE,"E1.bottom")])],"isStart":false});
            fillet(context, id + "F15", {"entities" : qUnion([Q0]), "radius" : 2 * mm, "tangentPropagation" : true, "allowEdgeOverflow" : false});
        }
        {
            var Q0;
            {var subQ0=sQuery(id+"F0.wireOp",EDGE,"E21.filletArc");var subQ1=sQuery(id+"F0.wireOp",EDGE,"E7");var subQ2=sQuery(id+"F0.wireOp",EDGE,"E6");var subQ3=sQuery(id+"F0.wireOp",EDGE,"E5");var subQ4=sQuery(id+"F0.wireOp",EDGE,"E4");var subQ5=sQuery(id+"F0.wireOp",EDGE,"E22.filletArc");var subQ6=sQuery(id+"F0.wireOp",EDGE,"E1.bottom");var subQ7=sQuery(id+"F0.wireOp",EDGE,"E1.right");var subQ8=sQuery(id+"F0.wireOp",EDGE,"E1.top");var subQ9=sQuery(id+"F0.wireOp",EDGE,"E1.left");var subQ10=sQuery(id+"F0.wireOp",EDGE,"E23.filletArc");var subQ11=sQuery(id+"F0.wireOp",EDGE,"E24.filletArc");Q0=makeQuery(id+"F2.boolean.opBoolean","SPLIT",FACE,{"disambiguationData":[TD([makeQuery(id+"F1.opExtrude","SWEPT_FACE",FACE,{"disambiguationData":[OSD([subQ6])]})])],"derivedFrom":makeQuery(id+"F1.opExtrude","CAP_FACE",FACE,{"disambiguationData":[OSD([subQ6,subQ8,subQ9,subQ7,subQ4,subQ3,subQ2,subQ1,subQ0,subQ5,subQ10,subQ11])],"isStart":true})});}
            var sketch = newSketch(context, id + "F16", { "sketchPlane" : qUnion([Q0])});
            skSolve(sketch);
        }
        {
            var Q0;
            {var subQ0=sQuery(id+"F0.wireOp",EDGE,"E21.filletArc");var subQ1=sQuery(id+"F0.wireOp",EDGE,"E7");var subQ2=sQuery(id+"F0.wireOp",EDGE,"E6");var subQ3=sQuery(id+"F0.wireOp",EDGE,"E5");var subQ4=sQuery(id+"F0.wireOp",EDGE,"E4");var subQ5=sQuery(id+"F0.wireOp",EDGE,"E22.filletArc");var subQ6=sQuery(id+"F0.wireOp",EDGE,"E1.bottom");var subQ7=sQuery(id+"F0.wireOp",EDGE,"E1.right");var subQ8=sQuery(id+"F0.wireOp",EDGE,"E1.top");var subQ9=sQuery(id+"F0.wireOp",EDGE,"E1.left");var subQ10=sQuery(id+"F0.wireOp",EDGE,"E23.filletArc");var subQ11=sQuery(id+"F0.wireOp",EDGE,"E24.filletArc");Q0=makeQuery(id+"F2.boolean.opBoolean","SPLIT",FACE,{"disambiguationData":[TD([makeQuery(id+"F1.opExtrude","SWEPT_FACE",FACE,{"disambiguationData":[OSD([subQ6])]})])],"derivedFrom":makeQuery(id+"F1.opExtrude","CAP_FACE",FACE,{"disambiguationData":[OSD([subQ6,subQ8,subQ9,subQ7,subQ4,subQ3,subQ2,subQ1,subQ0,subQ5,subQ10,subQ11])],"isStart":true})});}
            var sketch = newSketch(context, id + "F17", { "sketchPlane" : qUnion([Q0])});
            skLineSegment(sketch, "E79.0", {"start": v(-70, 90) * mm, "end": v(70, 90) * mm});
            skArc(sketch, "E79.1", {"start": v(-70, 90) * mm, "mid": v(-77.07, 87.07) * mm, "end": v(-80, 80) * mm});
            skLineSegment(sketch, "E79.2", {"start": v(-80, -80) * mm, "end": v(-80, 80) * mm});
            skArc(sketch, "E79.3", {"start": v(56.15, 48.18) * mm, "mid": v(0, 67.5) * mm, "end": v(-56.15, 48.18) * mm});
            skCircle(sketch, "E79.4", {"center": v(-60, 67.5) * mm, "radius": 4 * mm});
            skArc(sketch, "E79.5", {"start": v(-56.15, 48.18) * mm, "mid": v(-58.99, 44.68) * mm, "end": v(-60, 40.3) * mm});
            skArc(sketch, "E79.6", {"start": v(60, 40.3) * mm, "mid": v(58.99, 44.68) * mm, "end": v(56.15, 48.18) * mm});
            skLineSegment(sketch, "E79.7", {"start": v(60, 40.3) * mm, "end": v(60, -40.3) * mm});
            skArc(sketch, "E79.8", {"start": v(80, 80) * mm, "mid": v(77.07, 87.07) * mm, "end": v(70, 90) * mm});
            skLineSegment(sketch, "E79.9", {"start": v(80, -80) * mm, "end": v(80, 80) * mm});
            skLineSegment(sketch, "E79.10", {"start": v(-60, 40.3) * mm, "end": v(-60, -40.3) * mm});
            skArc(sketch, "E79.11", {"start": v(70, -90) * mm, "mid": v(77.07, -87.07) * mm, "end": v(80, -80) * mm});
            skLineSegment(sketch, "E79.12", {"start": v(-70, -90) * mm, "end": v(70, -90) * mm});
            skArc(sketch, "E79.13", {"start": v(-80, -80) * mm, "mid": v(-77.07, -87.07) * mm, "end": v(-70, -90) * mm});
            skCircle(sketch, "E79.14", {"center": v(-60, -67.5) * mm, "radius": 4 * mm});
            skCircle(sketch, "E79.15", {"center": v(60, -67.5) * mm, "radius": 4 * mm});
            skArc(sketch, "E79.16", {"start": v(-56.15, -48.18) * mm, "mid": v(0, -67.5) * mm, "end": v(56.15, -48.18) * mm});
            skArc(sketch, "E79.17", {"start": v(-60, -40.3) * mm, "mid": v(-58.99, -44.68) * mm, "end": v(-56.15, -48.18) * mm});
            skArc(sketch, "E79.18", {"start": v(56.15, -48.18) * mm, "mid": v(58.99, -44.68) * mm, "end": v(60, -40.3) * mm});
            skCircle(sketch, "E79.19", {"center": v(60, 67.5) * mm, "radius": 4 * mm});
            skPoint(sketch, "E79.20", {"position": v(77.07, 87.07) * mm});
            skLineSegment(sketch, "E80", {"start": v(0, 90) * mm, "end": v(0, 120) * mm, "construction": true});
            skLineSegment(sketch, "E81", {"start": v(-33, 90) * mm, "end": v(-15, 108) * mm});
            skCircle(sketch, "E82", {"center": v(0, 120) * mm, "radius": 6 * mm});
            skLineSegment(sketch, "E83", {"start": v(-15, 108) * mm, "end": v(-15, 120) * mm});
            skLineSegment(sketch, "E84", {"start": v(33, 90) * mm, "end": v(15, 108) * mm});
            skLineSegment(sketch, "E85", {"start": v(15, 108) * mm, "end": v(15, 120) * mm});
            skArc(sketch, "E86", {"start": v(-15, 120) * mm, "mid": v(0, 135) * mm, "end": v(15, 120) * mm});
            skLineSegment(sketch, "E87", {"start": v(-122.07, 0) * mm, "end": v(124.6, 0) * mm, "construction": true});
            skPoint(sketch, "E87.endSnap0", {"position": v(-60, 0) * mm});
            skLineSegment(sketch, "E88.MirrorCS", {"start": v(-33, -90) * mm, "end": v(-15, -108) * mm});
            skLineSegment(sketch, "E89.MirrorCS", {"start": v(-15, -108) * mm, "end": v(-15, -120) * mm});
            skArc(sketch, "E90.MirrorCS", {"start": v(-15, -120) * mm, "mid": v(0, -135) * mm, "end": v(15, -120) * mm});
            skLineSegment(sketch, "E91.MirrorCS", {"start": v(15, -108) * mm, "end": v(15, -120) * mm});
            skLineSegment(sketch, "E92.MirrorCS", {"start": v(33, -90) * mm, "end": v(15, -108) * mm});
            skCircle(sketch, "E93.MirrorC", {"center": v(0, -120) * mm, "radius": 6 * mm});
            skSolve(sketch);
        }
        {
            var Q0;
            {var subQ0=sQuery(id+"F17.wireOp",EDGE,"E81");Q0=makeQuery(id+"F17.imprint","IMPRINT",FACE,{"disambiguationData":[TD([[makeQuery(id+"F17.imprint","IMPRINT",EDGE,{"derivedFrom":subQ0}),-1.0]])]});}
            var Q1;
            Q1=makeQuery(id+"F16.imprint","IMPRINT",FACE,{"disambiguationData":[TD([[makeQuery(id+"F16.imprint","IMPRINT",EDGE,{"derivedFrom":makeQuery(id+"F1.opExtrude","CAP_EDGE",EDGE,{"disambiguationData":[OSD([sQuery(id+"F0.wireOp",EDGE,"E1.bottom")])],"isStart":true})}),1.0]])]});
            var Q2;
            {var subQ0=sQuery(id+"F17.wireOp",EDGE,"E88.MirrorCS");Q2=makeQuery(id+"F17.imprint","IMPRINT",FACE,{"disambiguationData":[TD([[makeQuery(id+"F17.imprint","IMPRINT",EDGE,{"derivedFrom":subQ0}),1.0]])]});}
            var Q3;
            Q3=makeQuery(id+"F2.opExtrude","CAP_FACE",FACE,{"disambiguationData":[OSD([sQuery(id+"F0.wireOp",EDGE,"E12"),sQuery(id+"F0.wireOp",EDGE,"E13"),sQuery(id+"F0.wireOp",EDGE,"E14"),sQuery(id+"F0.wireOp",EDGE,"E15"),sQuery(id+"F0.wireOp",EDGE,"E17.filletArc"),sQuery(id+"F0.wireOp",EDGE,"E18.filletArc"),sQuery(id+"F0.wireOp",EDGE,"E19.filletArc"),sQuery(id+"F0.wireOp",EDGE,"E20.filletArc"),sQuery(id+"F0.wireOp",EDGE,"E25.0"),sQuery(id+"F0.wireOp",EDGE,"E25.1"),sQuery(id+"F0.wireOp",EDGE,"E25.2"),sQuery(id+"F0.wireOp",EDGE,"E25.3"),sQuery(id+"F0.wireOp",EDGE,"E25.4"),sQuery(id+"F0.wireOp",EDGE,"E25.5"),sQuery(id+"F0.wireOp",EDGE,"E25.6"),sQuery(id+"F0.wireOp",EDGE,"E25.7")])],"isStart":false});
            extrude(context, id + "F18", {"entities" : qUnion([Q0, Q1, Q2]), "endBound" : BoundingType.UP_TO_SURFACE, "endBoundEntityFace" : qUnion([Q3]), "depth" : 25 * mm});
        }
    });
